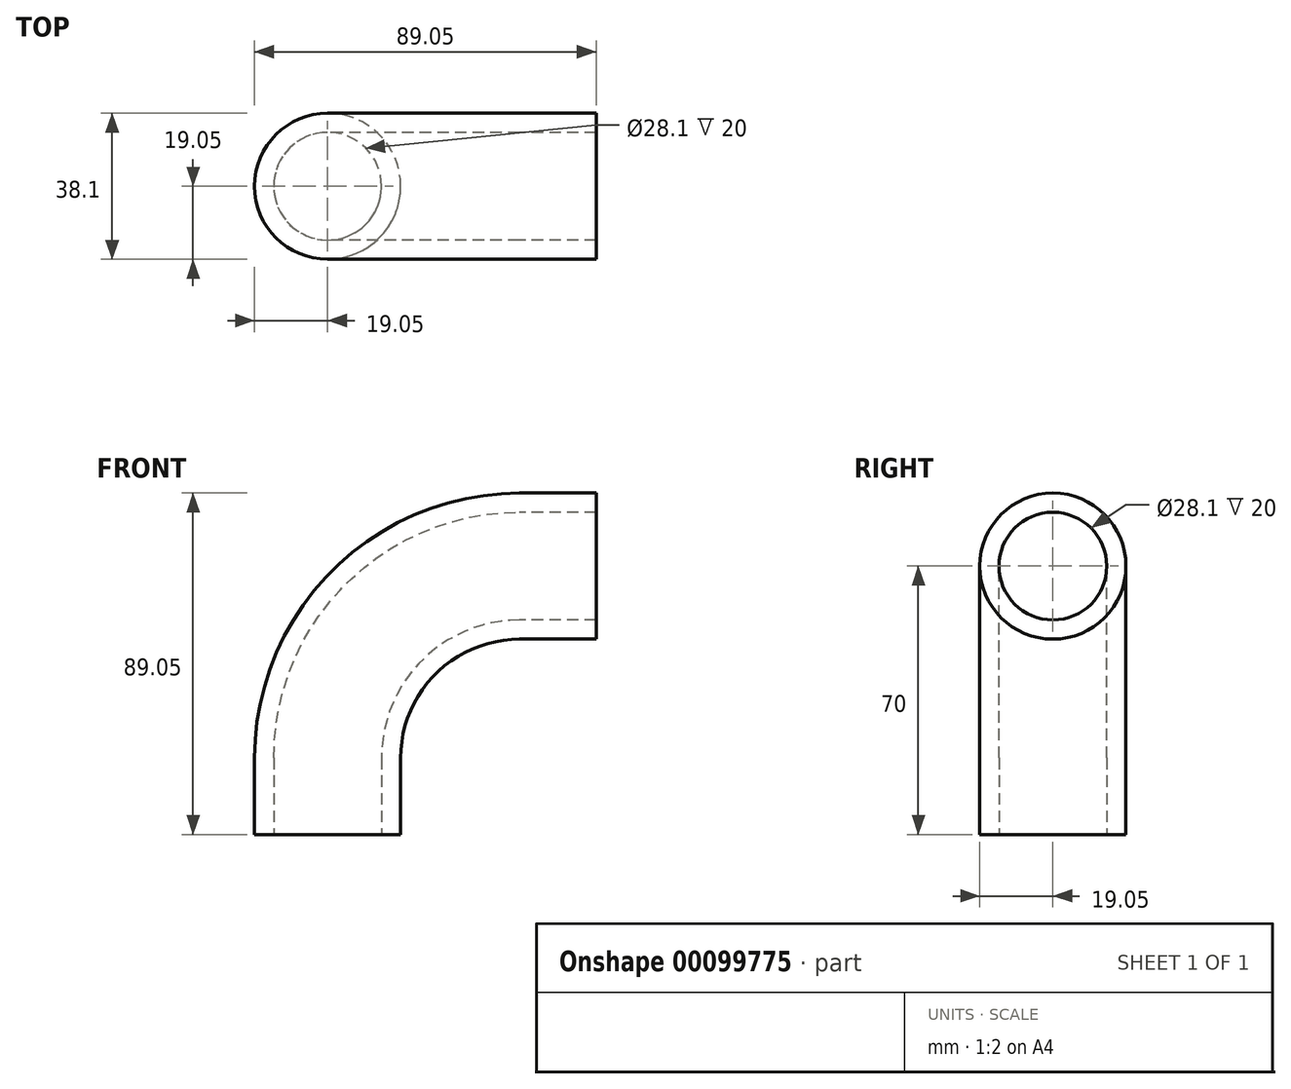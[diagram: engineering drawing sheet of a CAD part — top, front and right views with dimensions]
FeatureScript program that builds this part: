
annotation { "Feature Type Name" : "Feature", "Feature Type Description" : "" }
export const myFeature = defineFeature(function(context is Context, id is Id, definition is map)
    precondition{}
    {
        {
            var Q0;
            Q0=qCreatedBy(makeId("Front.planeOp"),FACE);
            var sketch = newSketch(context, id + "F0", { "sketchPlane" : qUnion([Q0])});
            skLineSegment(sketch, "E0", {"start": v(0, 0) * mm, "end": v(-20, 0) * mm});
            skLineSegment(sketch, "E1", {"start": v(-70, -50) * mm, "end": v(-70, -70) * mm});
            skPoint(sketch, "E2.visualSharp", {"position": v(-70, 0) * mm});
            skArc(sketch, "E2.filletArc", {"start": v(-20, 0) * mm, "mid": v(-55.36, -14.64) * mm, "end": v(-70, -50) * mm});
            skSolve(sketch);
        }
        {
            var Q0;
            Q0=qCreatedBy(makeId("Right.planeOp"),FACE);
            var sketch = newSketch(context, id + "F1", { "sketchPlane" : qUnion([Q0])});
            skCircle(sketch, "E3", {"center": v(0, 0) * mm, "radius": 19.05 * mm});
            skCircle(sketch, "E4", {"center": v(0, 0) * mm, "radius": 14.05 * mm});
            skSolve(sketch);
        }
        {
            var Q0;
            Q0 = qSketchRegion(id + "F1", true);
            var Q1;
            Q1=sQuery(id+"F0.wireOp",EDGE,"E0");
            var Q2;
            Q2=sQuery(id+"F0.wireOp",EDGE,"E2.filletArc");
            var Q3;
            Q3=sQuery(id+"F0.wireOp",EDGE,"E1");
            sweep(context, id + "F2", {"profiles" : qUnion([Q0]), "path" : qUnion([Q1, Q2, Q3])});
        }
    });
